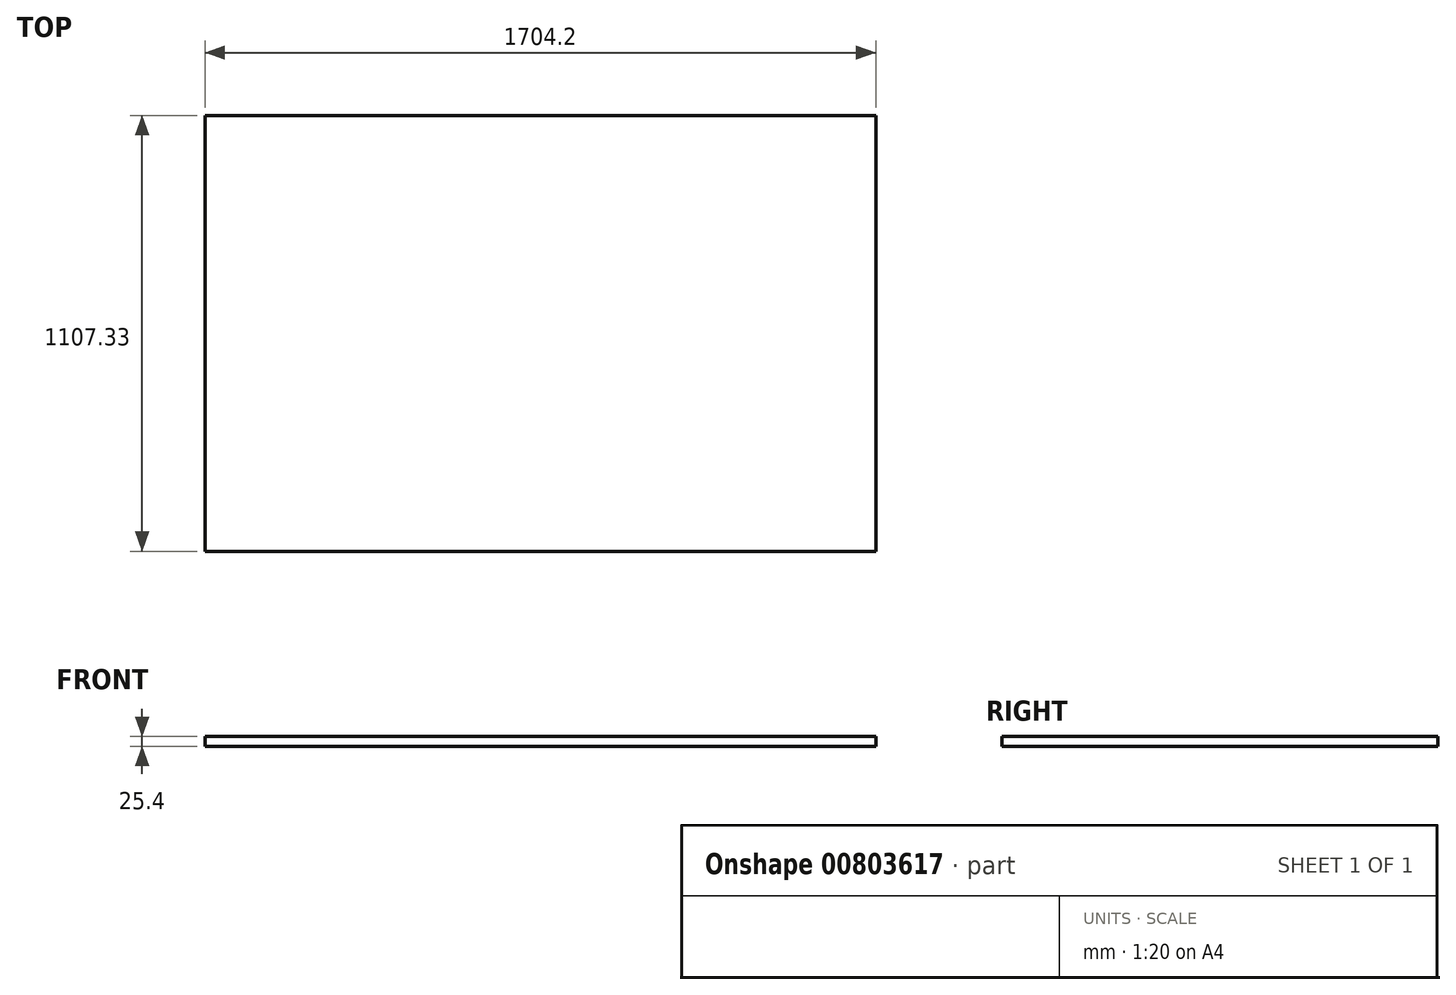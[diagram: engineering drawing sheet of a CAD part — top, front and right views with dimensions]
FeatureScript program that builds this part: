
annotation { "Feature Type Name" : "Feature", "Feature Type Description" : "" }
export const myFeature = defineFeature(function(context is Context, id is Id, definition is map)
    precondition{}
    {
        {
            var Q0;
            Q0=qCreatedBy(makeId("Top.planeOp"),FACE);
            var sketch = newSketch(context, id + "F0", { "sketchPlane" : qUnion([Q0])});
            skLineSegment(sketch, "E0.bottom", {"start": v(0, 0) * mm, "end": v(1704.2, 0) * mm});
            skLineSegment(sketch, "E0.top", {"start": v(0, 1107.33) * mm, "end": v(1704.2, 1107.33) * mm});
            skLineSegment(sketch, "E0.left", {"start": v(0, 0) * mm, "end": v(0, 1107.33) * mm});
            skLineSegment(sketch, "E0.right", {"start": v(1704.2, 0) * mm, "end": v(1704.2, 1107.33) * mm});
            skSolve(sketch);
        }
        {
            var Q0;
            Q0 = qSketchRegion(id + "F0", true);
            extrude(context, id + "F1", {"entities" : qUnion([Q0]), "depth" : 25.4 * mm, "offsetDistance" : 25.4 * mm});
        }
    });
